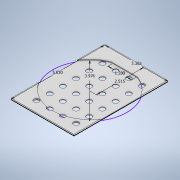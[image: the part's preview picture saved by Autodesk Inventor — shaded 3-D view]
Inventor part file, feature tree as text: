
AUTODESK INVENTOR PART (.ipt)
format: ipt  version: 2020 (Build 240168000, 168)  size: 195,584 bytes
history: native  units: in
note: dims shown in document units (in); Inventor stores cm internally (conversion verified against a paired STEP export)
features: sketch x2, extrude x2, hole x1, pattern_linear x1
ambient origin geometry x8: Origin, YZ Plane, XZ Plane, XY Plane, X Axis, Y Axis, Z Axis, Center Point
bodies: Solid1 (feature_tree)
feature tree (6):
  sketch  "Sketch1"  dims[d0=3.3654in d1=5.0299in]
  extrude  "Extrusion1"  Depth=5.0299in
  extrude  "Extrusion2"  Depth=0.0312in
  hole  "Hole1"  [1 undecoded]
  pattern_linear  "Rectangular Pattern1"  Spacing1=0.0706in  [1 undecoded]
  sketch  "Sketch2"  dims[d2=2.515in d3=3.9764in d4=1.2795in d5=0.0706in d6=0.0in d7=0.0312in d8=0.0in d9=0.2362in d10=0.0in d11=0.2756in d12=0.75in d13=0.438in d14=0.25in d15=0.5635in d16=1.0in d17=0.8108in d18=2.3622in d20=0.7087in d21=1.5748in d23=0.7087in d24=0.2362in d25=0.2362in d26=0.5661in d27=0.4465in]
note: 2 required parameter values undecoded (feature->parameter linkage not recoverable at this tier; creation-order binding heuristic only, values carry confidence <= 0.55)
